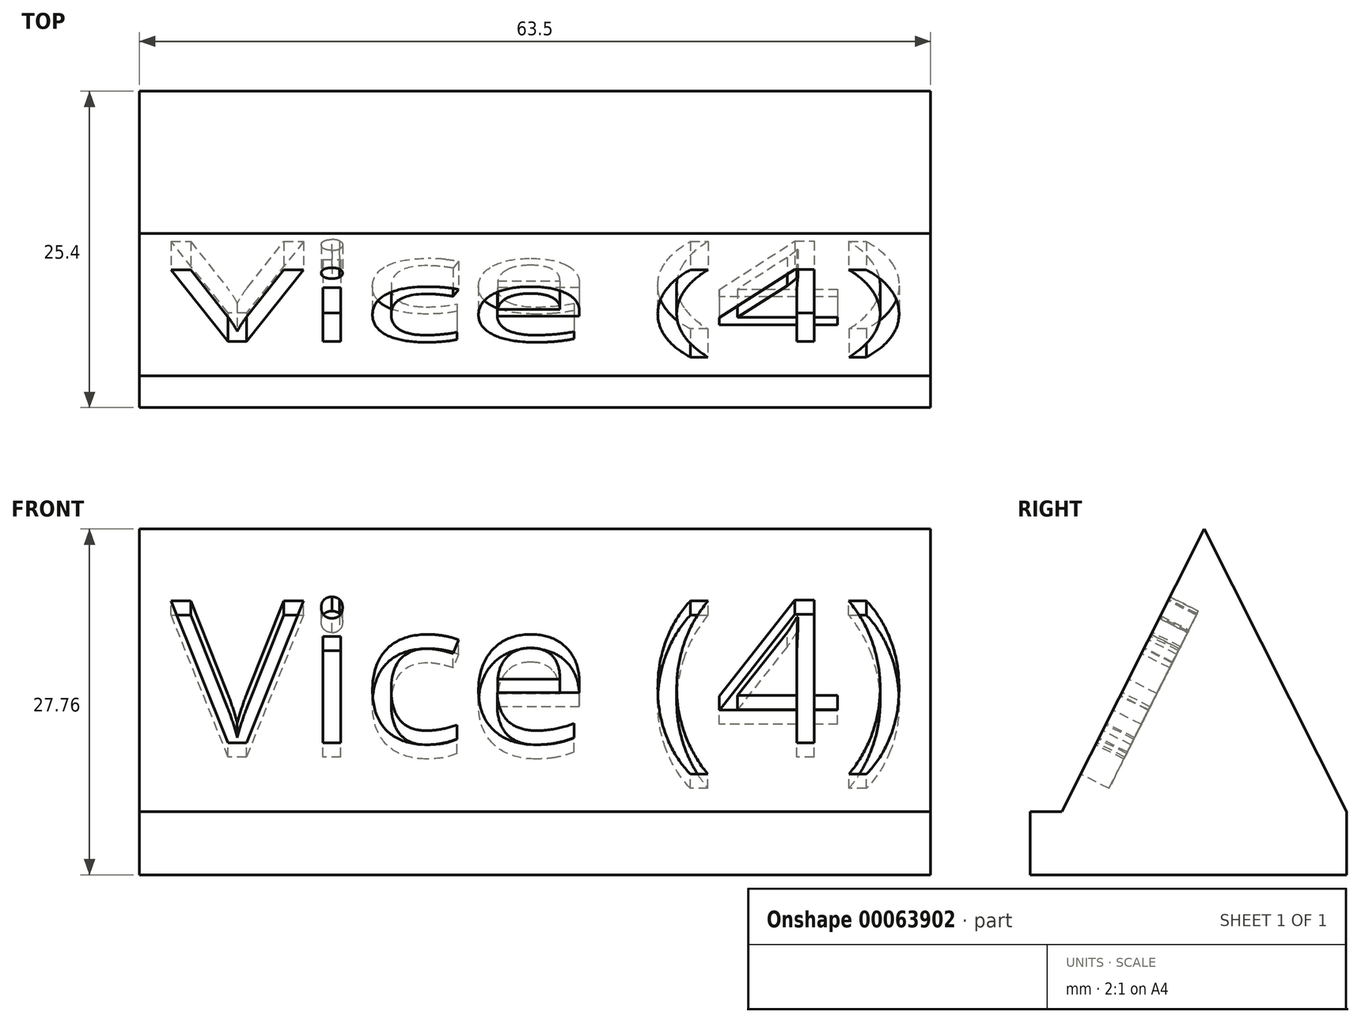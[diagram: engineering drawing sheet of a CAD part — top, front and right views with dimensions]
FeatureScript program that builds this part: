
annotation { "Feature Type Name" : "Feature", "Feature Type Description" : "" }
export const myFeature = defineFeature(function(context is Context, id is Id, definition is map)
    precondition{}
    {
        {
            var Q0;
            Q0=qCreatedBy(makeId("Right.planeOp"),FACE);
            var sketch = newSketch(context, id + "F0", { "sketchPlane" : qUnion([Q0])});
            skLineSegment(sketch, "E0", {"start": v(0, 0) * mm, "end": v(0, 5.08) * mm});
            skLineSegment(sketch, "E1", {"start": v(0, 5.08) * mm, "end": v(2.54, 5.08) * mm});
            skLineSegment(sketch, "E2", {"start": v(25.4, 5.08) * mm, "end": v(25.4, 5.08) * mm});
            skLineSegment(sketch, "E3", {"start": v(0, 0) * mm, "end": v(25.4, 0) * mm});
            skLineSegment(sketch, "E4", {"start": v(25.4, 0) * mm, "end": v(25.4, 5.08) * mm});
            skLineSegment(sketch, "E5", {"start": v(13.97, 27.76) * mm, "end": v(2.54, 5.08) * mm});
            skLineSegment(sketch, "E6", {"start": v(25.4, 5.08) * mm, "end": v(13.97, 27.76) * mm});
            skSolve(sketch);
        }
        {
            var Q0;
            Q0 = qSketchRegion(id + "F0", true);
            extrude(context, id + "F1", {"entities" : qUnion([Q0]), "depth" : 63.5 * mm});
        }
        {
            var Q0;
            Q0=makeQuery(id+"F1.opExtrude","SWEPT_FACE",FACE,{"disambiguationData":[OSD([sQuery(id+"F0.wireOp",EDGE,"E5")])]});
            var sketch = newSketch(context, id + "F2", { "sketchPlane" : qUnion([Q0])});
            skText(sketch, "E7", { "text": "Vice (4)", "fontName": "OpenSans-Regular.ttf"});
            const initialGuessF2  = {"E7": [0.00254, 0.01186, 1, 0, 0.01287]};
            skSetInitialGuess(sketch, initialGuessF2);
            skSolve(sketch);
        }
        {
            var Q0;
            Q0 = qSketchRegion(id + "F2", true);
            extrude(context, id + "F3", {"entities" : qUnion([Q0]), "operationType" : NewBodyOperationType.REMOVE, "oppositeDirection" : true, "depth" : 2.54 * mm});
        }
    });
